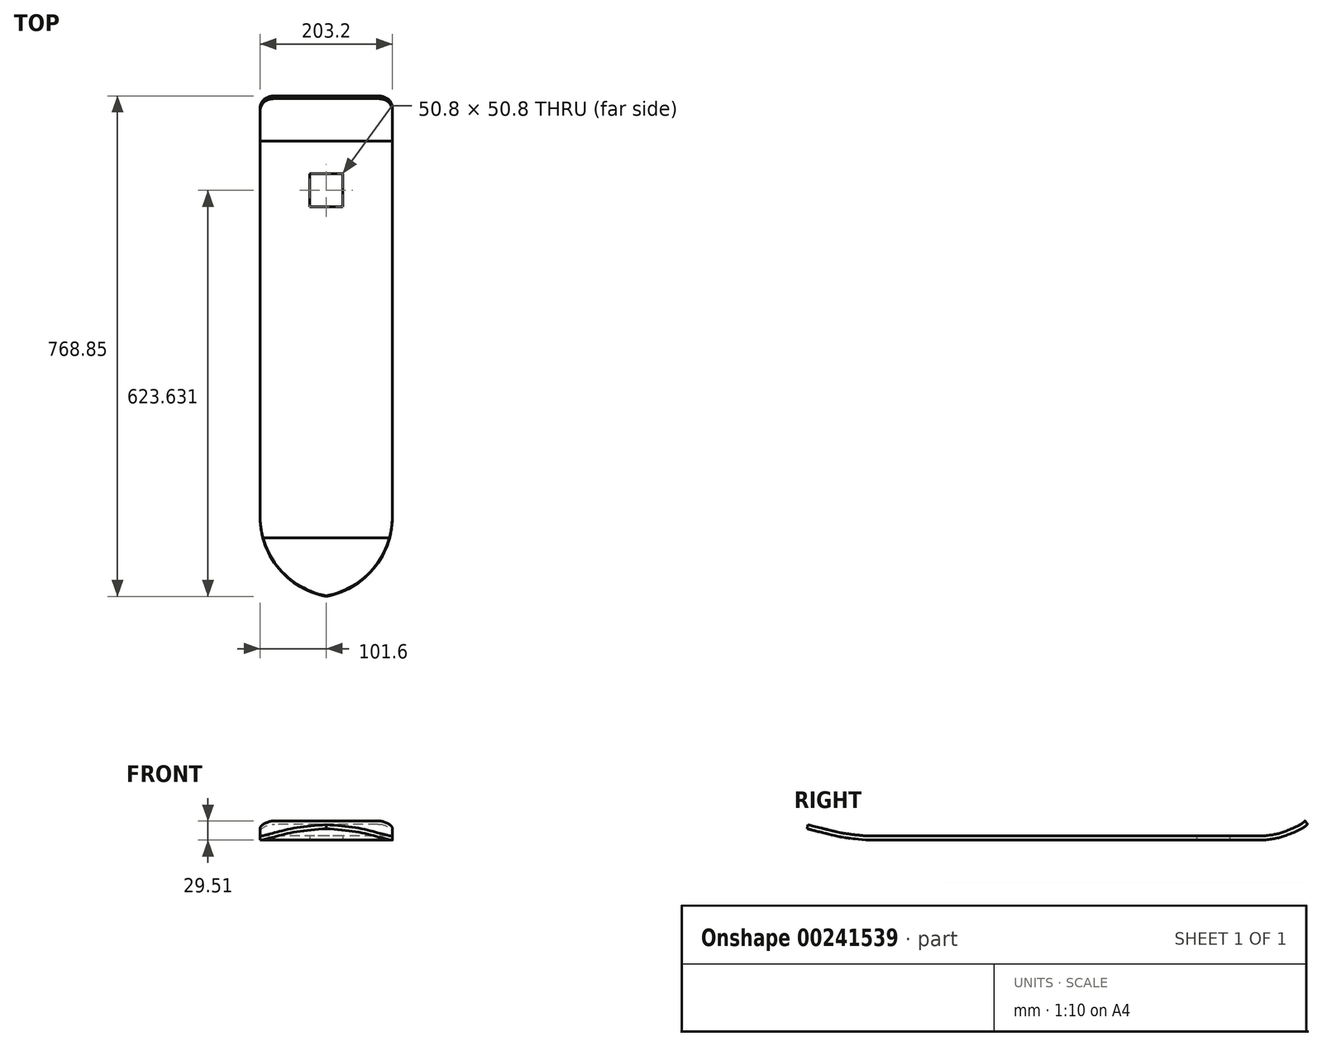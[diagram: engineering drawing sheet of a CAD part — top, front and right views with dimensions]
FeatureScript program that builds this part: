
annotation { "Feature Type Name" : "Feature", "Feature Type Description" : "" }
export const myFeature = defineFeature(function(context is Context, id is Id, definition is map)
    precondition{}
    {
        {
            var Q0;
            Q0=qCreatedBy(makeId("Top.planeOp"),FACE);
            var sketch = newSketch(context, id + "F0", { "sketchPlane" : qUnion([Q0])});
            skLineSegment(sketch, "E0.bottom", {"start": v(101.6, 304.8) * mm, "end": v(-101.6, 304.8) * mm});
            skLineSegment(sketch, "E0.top", {"start": v(101.6, -304.8) * mm, "end": v(-101.6, -304.8) * mm});
            skLineSegment(sketch, "E0.left", {"start": v(101.6, 304.8) * mm, "end": v(101.6, -304.8) * mm});
            skLineSegment(sketch, "E0.right", {"start": v(-101.6, 304.8) * mm, "end": v(-101.6, -304.8) * mm});
            skPoint(sketch, "E0.middle", {"position": v(0, 0) * mm});
            skLineSegment(sketch, "E1.bottom", {"start": v(25.4, 203.3) * mm, "end": v(-25.4, 203.3) * mm});
            skLineSegment(sketch, "E1.top", {"start": v(25.4, 254.1) * mm, "end": v(-25.4, 254.1) * mm});
            skLineSegment(sketch, "E1.left", {"start": v(25.4, 203.3) * mm, "end": v(25.4, 254.1) * mm});
            skLineSegment(sketch, "E1.right", {"start": v(-25.4, 203.3) * mm, "end": v(-25.4, 254.1) * mm});
            skPoint(sketch, "E1.middle", {"position": v(0, 228.7) * mm});
            skCircle(sketch, "E2", {"center": v(-19.05, 247.74) * mm, "radius": 3.18 * mm});
            skCircle(sketch, "E3", {"center": v(19.05, 247.74) * mm, "radius": 3.18 * mm});
            skCircle(sketch, "E4", {"center": v(-19.14, 209.64) * mm, "radius": 3.18 * mm});
            skCircle(sketch, "E5", {"center": v(19.05, 209.64) * mm, "radius": 3.18 * mm});
            skSolve(sketch);
        }
        {
            var Q0;
            Q0 = qSketchRegion(id + "F0", true);
            extrude(context, id + "F1", {"entities" : qUnion([Q0]), "endBound" : BoundingType.SYMMETRIC, "depth" : 6.35 * mm});
        }
        {
            var Q0;
            Q0=qCreatedBy(makeId("Right.planeOp"),FACE);
            var sketch = newSketch(context, id + "F2", { "sketchPlane" : qUnion([Q0])});
            skFitSpline(sketch, "E6", {"points": [v(305.22, 0) * mm, v(325.95, 2.85) * mm, v(343.4, 8.46) * mm, v(365.7, 18.68) * mm, v(372.17, 24.16) * mm], "startDerivative": vector(79.2, 8.22) * mm, "endDerivative": vector(28.92, 30.28) * mm});
            skSolve(sketch);
        }
        {
            var Q0;
            Q0=makeQuery(id+"F1.opExtrude","SWEPT_FACE",FACE,{"disambiguationData":[OSD([sQuery(id+"F0.wireOp",EDGE,"E0.bottom")])]});
            var Q1;
            Q1=sQuery(id+"F2.wireOp",EDGE,"E6");
            sweep(context, id + "F3", {"operationType" : NewBodyOperationType.ADD, "profiles" : qUnion([Q0]), "path" : qUnion([Q1])});
        }
        {
            var Q0;
            Q0=qCreatedBy(makeId("Right.planeOp"),FACE);
            var sketch = newSketch(context, id + "F4", { "sketchPlane" : qUnion([Q0])});
            skFitSpline(sketch, "E7", {"points": [v(-304.5, 0) * mm, v(-337.62, 4.01) * mm, v(-357.68, 8.21) * mm, v(-396.87, 18.01) * mm], "startDerivative": vector(-103.69, 11.06) * mm, "endDerivative": vector(-113.04, 28.55) * mm});
            skSolve(sketch);
        }
        {
            var Q0;
            Q0=makeQuery(id+"F1.opExtrude","SWEPT_FACE",FACE,{"disambiguationData":[OSD([sQuery(id+"F0.wireOp",EDGE,"E0.top")])]});
            var Q1;
            Q1=sQuery(id+"F4.wireOp",EDGE,"E7");
            sweep(context, id + "F5", {"operationType" : NewBodyOperationType.ADD, "profiles" : qUnion([Q0]), "path" : qUnion([Q1])});
        }
        {
            var Q0;
            Q0=makeQuery(id+"F5.opSweep","CAP_EDGE",EDGE,{"disambiguationData":[OSD([sQuery(id+"F0.wireOp",EDGE,"E0.top"),sQuery(id+"F0.wireOp",EDGE,"E0.right"),sQuery(id+"F4.wireOp",VERTEX,"E7.end")])],"isStart":false});
            var Q1;
            Q1=makeQuery(id+"F5.opSweep","CAP_EDGE",EDGE,{"disambiguationData":[OSD([sQuery(id+"F0.wireOp",EDGE,"E0.top"),sQuery(id+"F0.wireOp",EDGE,"E0.left"),sQuery(id+"F4.wireOp",VERTEX,"E7.end")])],"isStart":false});
            fillet(context, id + "F6", {"entities" : qUnion([Q0, Q1]), "radius" : 126.32 * mm, "tangentPropagation" : true, "allowEdgeOverflow" : false});
        }
        {
            var Q0;
            Q0=makeQuery(id+"F3.opSweep","CAP_EDGE",EDGE,{"disambiguationData":[OSD([sQuery(id+"F0.wireOp",EDGE,"E0.bottom"),sQuery(id+"F0.wireOp",EDGE,"E0.right"),sQuery(id+"F2.wireOp",VERTEX,"E6.end")])],"isStart":false});
            var Q1;
            Q1=makeQuery(id+"F3.opSweep","CAP_EDGE",EDGE,{"disambiguationData":[OSD([sQuery(id+"F0.wireOp",EDGE,"E0.bottom"),sQuery(id+"F0.wireOp",EDGE,"E0.left"),sQuery(id+"F2.wireOp",VERTEX,"E6.end")])],"isStart":false});
            fillet(context, id + "F7", {"entities" : qUnion([Q0, Q1]), "radius" : 22.08 * mm, "tangentPropagation" : true, "allowEdgeOverflow" : false});
        }
    });
